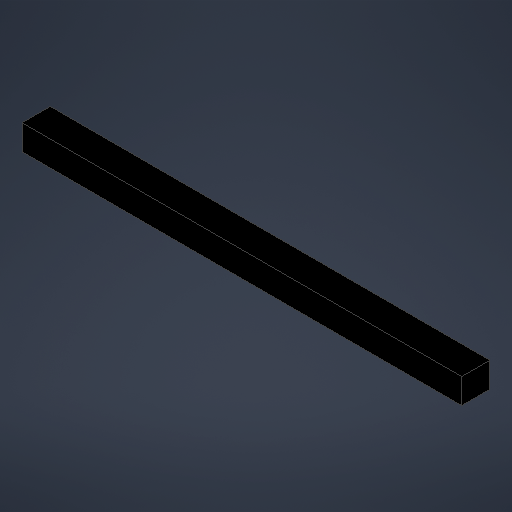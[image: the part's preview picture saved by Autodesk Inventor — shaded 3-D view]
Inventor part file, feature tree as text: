
AUTODESK INVENTOR PART (.ipt)
format: ipt  version: 2025.1 (Build 291241000, 241)  size: 188,416 bytes
history: native  units: mm
features: extrude x1, sketch x1
ambient origin geometry x8: Origin, YZ Plane, XZ Plane, XY Plane, X Axis, Y Axis, Z Axis, Center Point
bodies: Solid1 (feature_tree)
feature tree (2):
  extrude  "Extrusion1"  Depth=700.0mm
  sketch  "Sketch1"  dims[d0=45.0mm d1=700.0mm d2=40.0mm d3=0.0mm]
